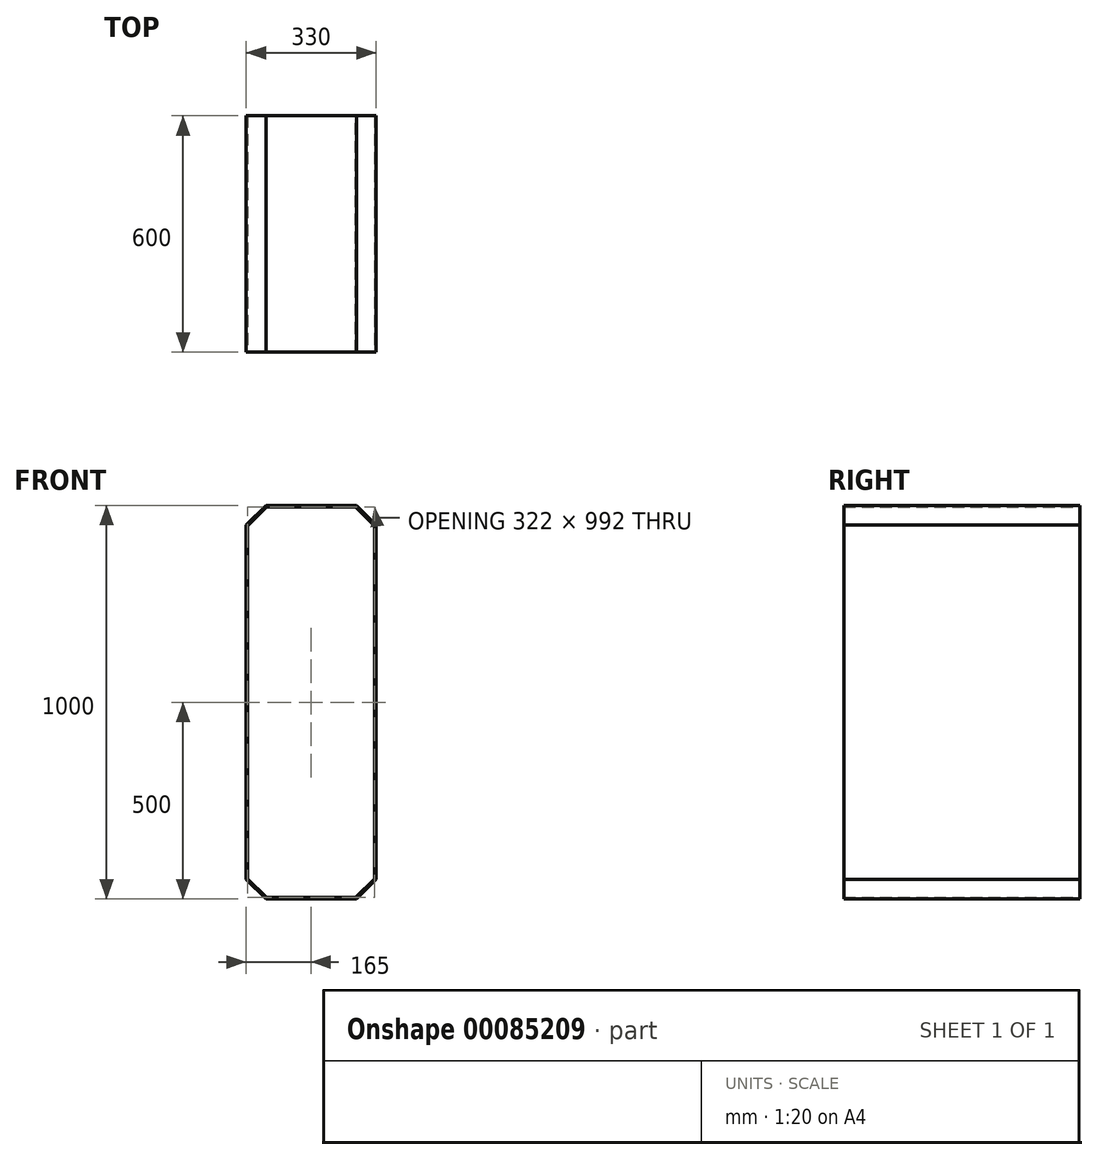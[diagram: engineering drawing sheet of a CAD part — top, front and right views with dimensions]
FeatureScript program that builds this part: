
annotation { "Feature Type Name" : "Feature", "Feature Type Description" : "" }
export const myFeature = defineFeature(function(context is Context, id is Id, definition is map)
    precondition{}
    {
        {
            var Q0;
            Q0=qCreatedBy(makeId("Front.planeOp"),FACE);
            var sketch = newSketch(context, id + "F0", { "sketchPlane" : qUnion([Q0])});
            skLineSegment(sketch, "E0.bottom", {"start": v(0, 0) * mm, "end": v(330, 0) * mm});
            skLineSegment(sketch, "E0.top", {"start": v(0, 1000) * mm, "end": v(330, 1000) * mm});
            skLineSegment(sketch, "E0.left", {"start": v(0, 0) * mm, "end": v(0, 1000) * mm});
            skLineSegment(sketch, "E0.right", {"start": v(330, 0) * mm, "end": v(330, 1000) * mm});
            skSolve(sketch);
        }
        {
            var Q0;
            Q0=makeQuery(id+"F0.imprint","IMPRINT",FACE,{"disambiguationData":[TD([[makeQuery(id+"F0.imprint","IMPRINT",EDGE,{"derivedFrom":sQuery(id+"F0.wireOp",EDGE,"E0.bottom")}),1.0]])]});
            extrude(context, id + "F1", {"entities" : qUnion([Q0]), "depth" : 600 * mm});
        }
        {
            var Q0;
            Q0=makeQuery(id+"F1.opExtrude","SWEPT_EDGE",EDGE,{"disambiguationData":[OSD([sQuery(id+"F0.wireOp",EDGE,"E0.top"),sQuery(id+"F0.wireOp",EDGE,"E0.left")])]});
            var Q1;
            Q1=makeQuery(id+"F1.opExtrude","SWEPT_EDGE",EDGE,{"disambiguationData":[OSD([sQuery(id+"F0.wireOp",EDGE,"E0.top"),sQuery(id+"F0.wireOp",EDGE,"E0.right")])]});
            var Q2;
            Q2=makeQuery(id+"F1.opExtrude","SWEPT_EDGE",EDGE,{"disambiguationData":[OSD([sQuery(id+"F0.wireOp",EDGE,"E0.bottom"),sQuery(id+"F0.wireOp",EDGE,"E0.left")])]});
            var Q3;
            Q3=makeQuery(id+"F1.opExtrude","SWEPT_EDGE",EDGE,{"disambiguationData":[OSD([sQuery(id+"F0.wireOp",EDGE,"E0.bottom"),sQuery(id+"F0.wireOp",EDGE,"E0.right")])]});
            chamfer(context, id + "F2", {"entities" : qUnion([Q0, Q1, Q2, Q3]), "width" : 50 * mm, "tangentPropagation" : true});
        }
        {
            var Q0;
            Q0=makeQuery(id+"F1.opExtrude","CAP_FACE",FACE,{"disambiguationData":[OSD([sQuery(id+"F0.wireOp",EDGE,"E0.bottom"),sQuery(id+"F0.wireOp",EDGE,"E0.top"),sQuery(id+"F0.wireOp",EDGE,"E0.left"),sQuery(id+"F0.wireOp",EDGE,"E0.right")])],"isStart":false});
            var Q1;
            Q1=makeQuery(id+"F1.opExtrude","CAP_FACE",FACE,{"disambiguationData":[OSD([sQuery(id+"F0.wireOp",EDGE,"E0.bottom"),sQuery(id+"F0.wireOp",EDGE,"E0.top"),sQuery(id+"F0.wireOp",EDGE,"E0.left"),sQuery(id+"F0.wireOp",EDGE,"E0.right")])],"isStart":true});
            shell(context, id + "F3", {"entities" : qUnion([Q0, Q1]), "thickness" : 4 * mm});
        }
    });
